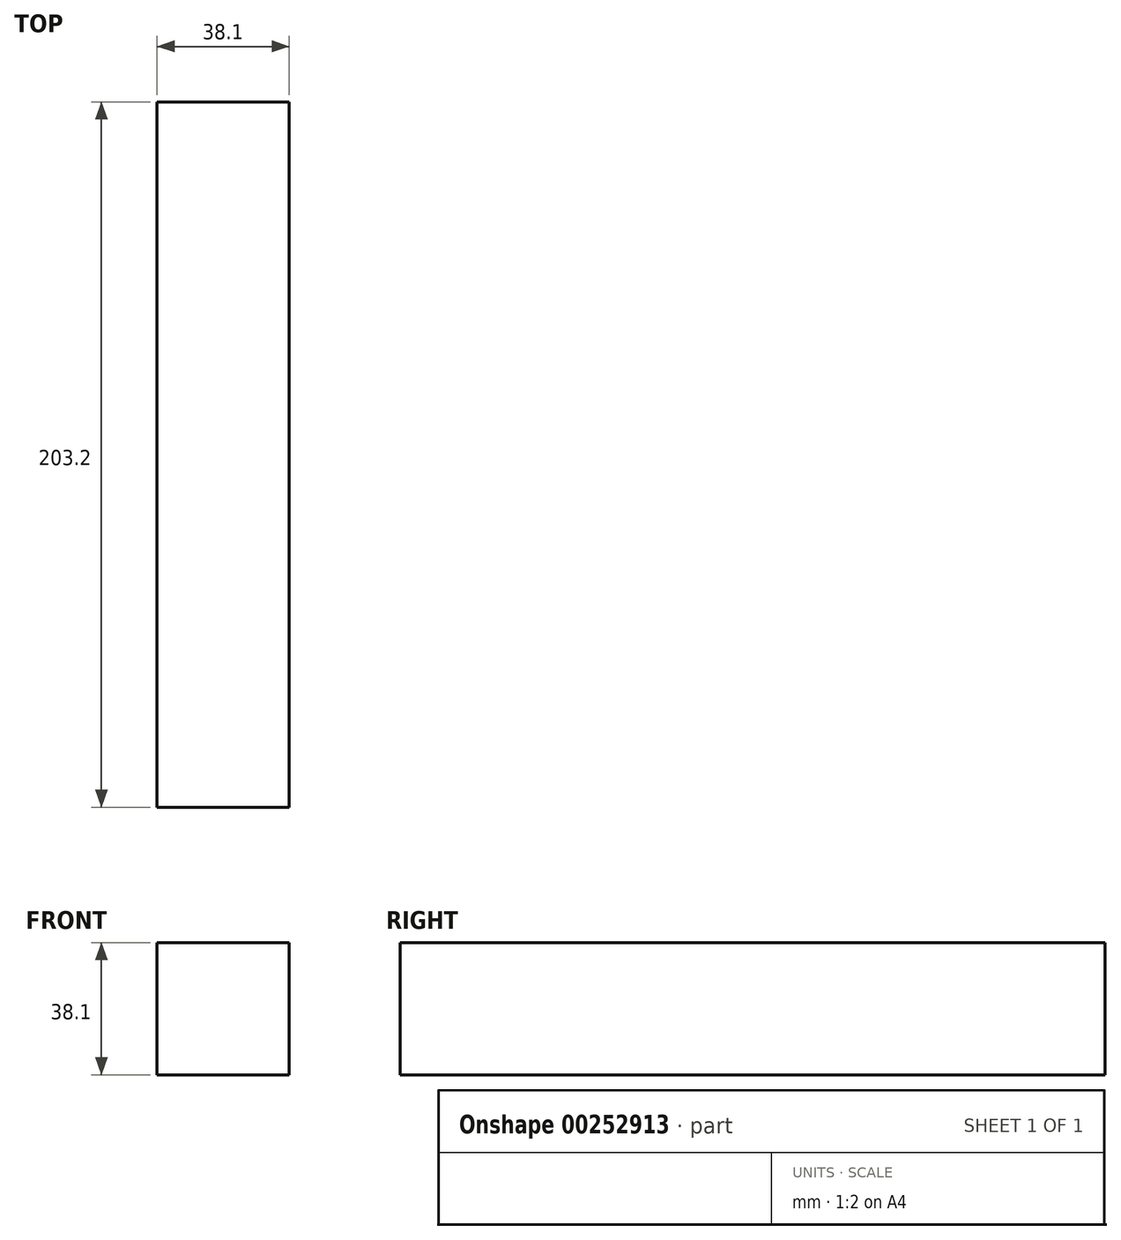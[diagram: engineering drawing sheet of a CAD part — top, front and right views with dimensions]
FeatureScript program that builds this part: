
annotation { "Feature Type Name" : "Feature", "Feature Type Description" : "" }
export const myFeature = defineFeature(function(context is Context, id is Id, definition is map)
    precondition{}
    {
        {
            var Q0;
            Q0=qCreatedBy(makeId("Front.planeOp"),FACE);
            var sketch = newSketch(context, id + "F0", { "sketchPlane" : qUnion([Q0])});
            skLineSegment(sketch, "E0", {"start": v(0, 0) * mm, "end": v(38.1, 0) * mm});
            skLineSegment(sketch, "E1", {"start": v(38.1, 0) * mm, "end": v(38.1, 38.1) * mm});
            skLineSegment(sketch, "E2", {"start": v(38.1, 38.1) * mm, "end": v(0, 38.1) * mm});
            skLineSegment(sketch, "E3", {"start": v(0, 38.1) * mm, "end": v(0, 0) * mm});
            skSolve(sketch);
        }
        {
            var Q0;
            Q0=makeQuery(id+"F0.imprint","IMPRINT",FACE,{"disambiguationData":[TD([[makeQuery(id+"F0.imprint","IMPRINT",EDGE,{"derivedFrom":sQuery(id+"F0.wireOp",EDGE,"E0")}),1.0]])]});
            extrude(context, id + "F1", {"entities" : qUnion([Q0]), "depth" : 203.2 * mm});
        }
    });
